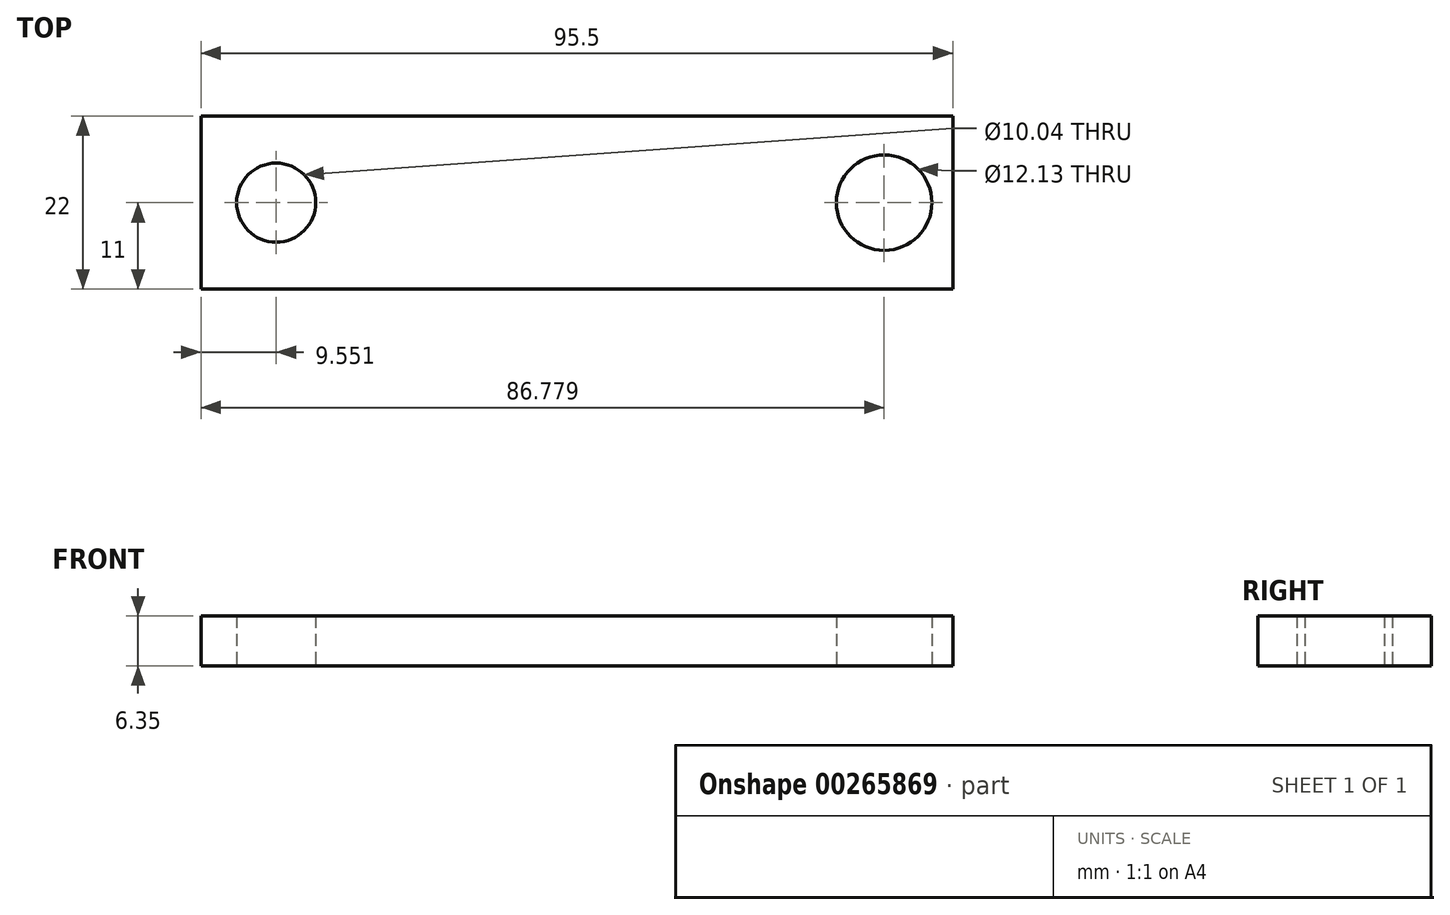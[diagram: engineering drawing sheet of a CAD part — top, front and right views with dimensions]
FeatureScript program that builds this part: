
annotation { "Feature Type Name" : "Feature", "Feature Type Description" : "" }
export const myFeature = defineFeature(function(context is Context, id is Id, definition is map)
    precondition{}
    {
        {
            var Q0;
            Q0=qCreatedBy(makeId("Top.planeOp"),FACE);
            var sketch = newSketch(context, id + "F0", { "sketchPlane" : qUnion([Q0])});
            skLineSegment(sketch, "E0.bottom", {"start": v(47.75, -11) * mm, "end": v(-47.75, -11) * mm});
            skLineSegment(sketch, "E0.top", {"start": v(47.75, 11) * mm, "end": v(-47.75, 11) * mm});
            skLineSegment(sketch, "E0.left", {"start": v(47.75, -11) * mm, "end": v(47.75, 11) * mm});
            skLineSegment(sketch, "E0.right", {"start": v(-47.75, -11) * mm, "end": v(-47.75, 11) * mm});
            skPoint(sketch, "E0.middle", {"position": v(0, 0) * mm});
            skCircle(sketch, "E1", {"center": v(-38.2, 0) * mm, "radius": 5.02 * mm});
            skCircle(sketch, "E2", {"center": v(39.03, 0) * mm, "radius": 6.06 * mm});
            skSolve(sketch);
        }
        {
            var Q0;
            Q0 = qSketchRegion(id + "F0", true);
            extrude(context, id + "F1", {"entities" : qUnion([Q0]), "depth" : 6.35 * mm});
        }
    });
